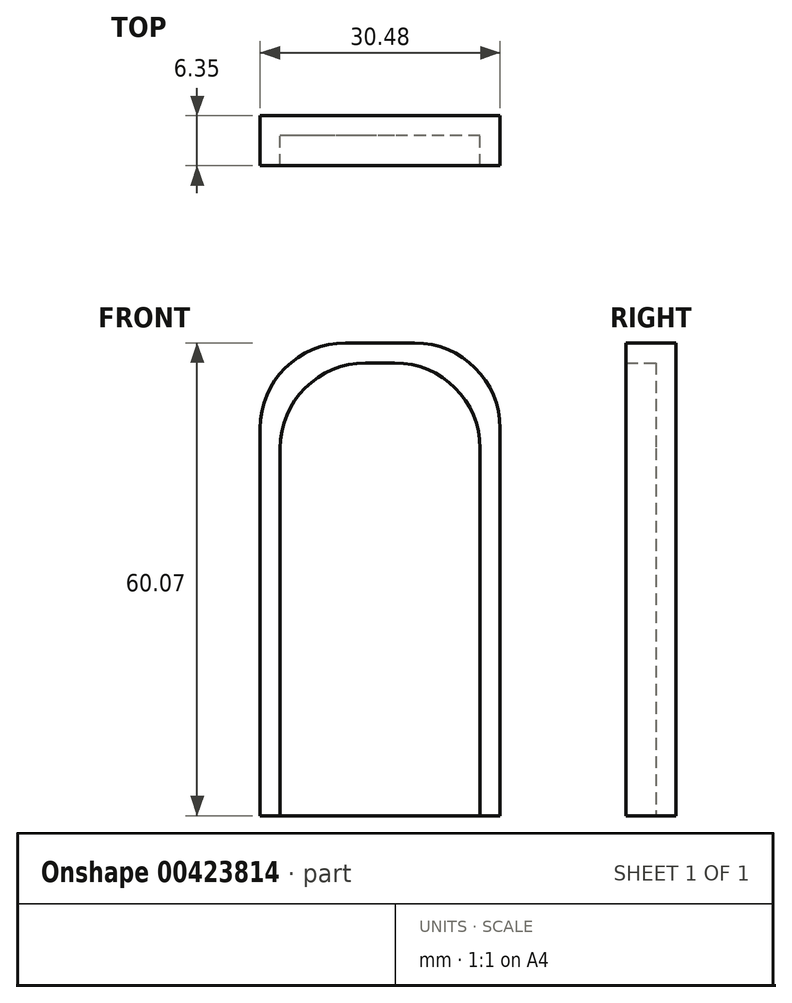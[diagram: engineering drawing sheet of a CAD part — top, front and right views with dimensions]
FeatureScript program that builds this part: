
annotation { "Feature Type Name" : "Feature", "Feature Type Description" : "" }
export const myFeature = defineFeature(function(context is Context, id is Id, definition is map)
    precondition{}
    {
        {
            var Q0;
            Q0=qCreatedBy(makeId("Front.planeOp"),FACE);
            var sketch = newSketch(context, id + "F0", { "sketchPlane" : qUnion([Q0])});
            skLineSegment(sketch, "E0.top", {"start": v(-10.87, 55) * mm, "end": v(-14.53, 55) * mm});
            skLineSegment(sketch, "E0.left", {"start": v(0, 0) * mm, "end": v(0, 44.12) * mm});
            skLineSegment(sketch, "E0.right", {"start": v(-25.4, 0) * mm, "end": v(-25.4, 44.12) * mm});
            skPoint(sketch, "E1.visualSharp", {"position": v(-25.4, 55) * mm});
            skArc(sketch, "E1.filletArc", {"start": v(-14.53, 55) * mm, "mid": v(-22.22, 51.8) * mm, "end": v(-25.4, 44.12) * mm});
            skPoint(sketch, "E2.visualSharp", {"position": v(0, 55) * mm});
            skArc(sketch, "E2.filletArc", {"start": v(0, 44.12) * mm, "mid": v(-3.18, 51.8) * mm, "end": v(-10.87, 55) * mm});
            skLineSegment(sketch, "E3", {"start": v(0, 0) * mm, "end": v(2.54, 0) * mm});
            skLineSegment(sketch, "E4", {"start": v(2.54, -2.54) * mm, "end": v(2.54, 0) * mm});
            skLineSegment(sketch, "E5", {"start": v(-10.87, 55) * mm, "end": v(-10.87, 57.53) * mm});
            skLineSegment(sketch, "E6", {"start": v(-10.87, 57.53) * mm, "end": v(-8.33, 57.53) * mm});
            skLineSegment(sketch, "E7", {"start": v(2.54, 46.66) * mm, "end": v(2.54, -2.54) * mm});
            skLineSegment(sketch, "E8", {"start": v(-25.4, 0) * mm, "end": v(-27.94, 0) * mm});
            skLineSegment(sketch, "E9", {"start": v(-27.94, 0) * mm, "end": v(-27.94, -2.54) * mm});
            skLineSegment(sketch, "E10", {"start": v(-27.94, -2.54) * mm, "end": v(-27.94, 46.66) * mm});
            skLineSegment(sketch, "E11", {"start": v(-17.07, 57.53) * mm, "end": v(-10.87, 57.53) * mm});
            skPoint(sketch, "E12.visualSharp", {"position": v(2.54, 57.53) * mm});
            skArc(sketch, "E12.filletArc", {"start": v(2.54, 46.66) * mm, "mid": v(-0.64, 54.35) * mm, "end": v(-8.33, 57.53) * mm});
            skPoint(sketch, "E13.visualSharp", {"position": v(-27.94, 57.53) * mm});
            skArc(sketch, "E13.filletArc", {"start": v(-17.07, 57.53) * mm, "mid": v(-24.76, 54.35) * mm, "end": v(-27.94, 46.66) * mm});
            skLineSegment(sketch, "E14", {"start": v(0, 0) * mm, "end": v(0, -2.54) * mm});
            skLineSegment(sketch, "E15", {"start": v(0, -2.54) * mm, "end": v(2.54, -2.54) * mm});
            skLineSegment(sketch, "E16", {"start": v(-25.4, 0) * mm, "end": v(-25.4, -2.54) * mm});
            skLineSegment(sketch, "E17", {"start": v(-25.4, -2.54) * mm, "end": v(-27.94, -2.54) * mm});
            skLineSegment(sketch, "E18", {"start": v(2.54, 0) * mm, "end": v(0, 0) * mm});
            skSolve(sketch);
        }
        {
            var Q0;
            Q0 = qSketchRegion(id + "F0", true);
            var Q1;
            Q1 = qSketchRegion(id + "F2", true);
            extrude(context, id + "F1", {"entities" : qUnion([Q0, Q1]), "depth" : 6.35 * mm});
        }
        {
            var Q0;
            Q0=qCreatedBy(makeId("Front.planeOp"),FACE);
            var sketch = newSketch(context, id + "F2", { "sketchPlane" : qUnion([Q0])});
            skLineSegment(sketch, "E19.bottom", {"start": v(0, 0) * mm, "end": v(-21.1, 0) * mm});
            skLineSegment(sketch, "E20", {"start": v(0, 0) * mm, "end": v(0, -2.54) * mm});
            skLineSegment(sketch, "E21", {"start": v(0, -2.54) * mm, "end": v(2.54, -2.54) * mm});
            skLineSegment(sketch, "E22", {"start": v(2.54, -2.54) * mm, "end": v(2.54, 46.66) * mm});
            skLineSegment(sketch, "E23", {"start": v(2.54, -2.54) * mm, "end": v(-27.94, -2.54) * mm});
            skLineSegment(sketch, "E24", {"start": v(-27.94, -2.54) * mm, "end": v(-27.94, 46.66) * mm});
            skLineSegment(sketch, "E25", {"start": v(-17.07, 57.53) * mm, "end": v(-8.33, 57.53) * mm});
            skPoint(sketch, "E26.visualSharp", {"position": v(-27.94, 57.53) * mm});
            skArc(sketch, "E26.filletArc", {"start": v(-17.07, 57.53) * mm, "mid": v(-24.76, 54.35) * mm, "end": v(-27.94, 46.66) * mm});
            skPoint(sketch, "E27.visualSharp", {"position": v(2.54, 57.53) * mm});
            skArc(sketch, "E27.filletArc", {"start": v(2.54, 46.66) * mm, "mid": v(-0.64, 54.35) * mm, "end": v(-8.33, 57.53) * mm});
            skSolve(sketch);
        }
        {
            var Q0;
            Q0 = qSketchRegion(id + "F2", true);
            extrude(context, id + "F3", {"entities" : qUnion([Q0]), "operationType" : NewBodyOperationType.ADD, "depth" : 2.54 * mm});
        }
    });
